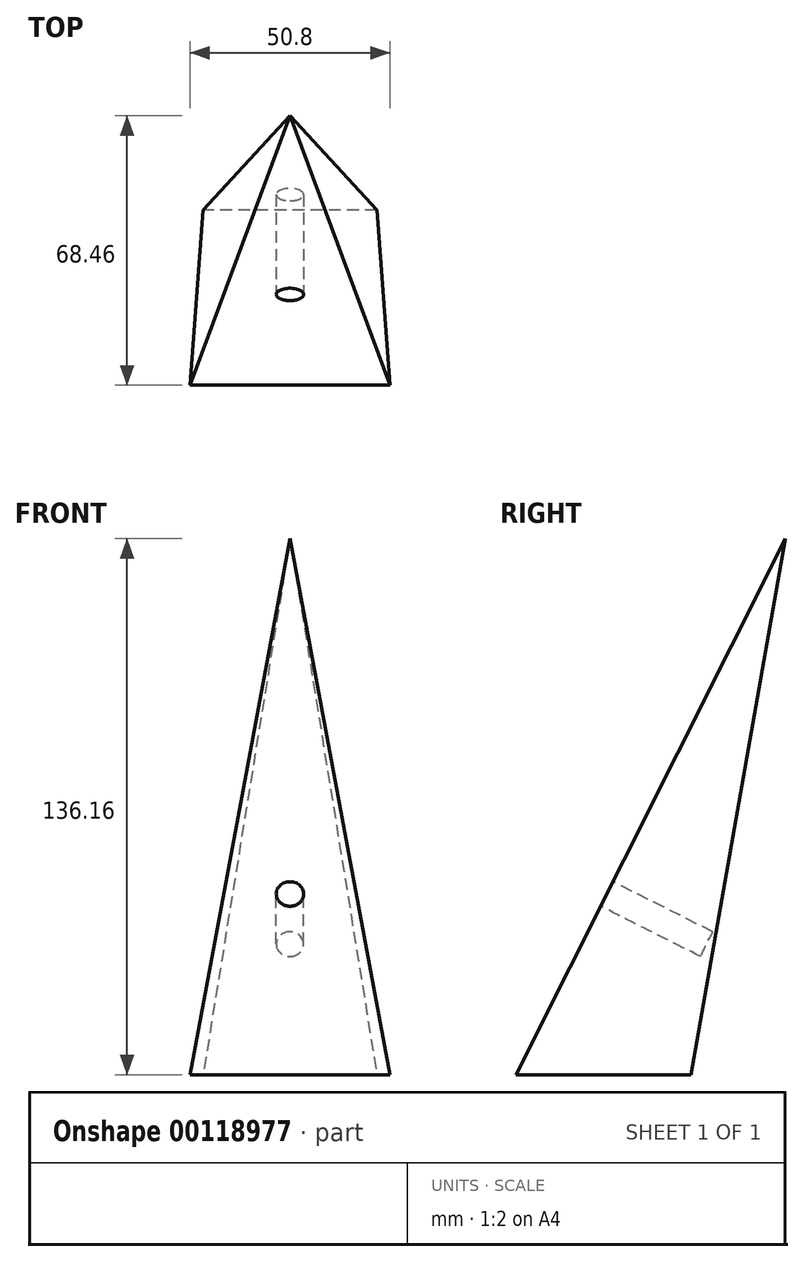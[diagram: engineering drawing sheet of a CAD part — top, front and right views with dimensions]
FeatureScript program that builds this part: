
annotation { "Feature Type Name" : "Feature", "Feature Type Description" : "" }
export const myFeature = defineFeature(function(context is Context, id is Id, definition is map)
    precondition{}
    {
        {
            var Q0;
            Q0=qCreatedBy(makeId("Right.planeOp"),FACE);
            var sketch = newSketch(context, id + "F0", { "sketchPlane" : qUnion([Q0])});
            skLineSegment(sketch, "E0", {"start": v(-22.3, 0) * mm, "end": v(22.16, 0) * mm});
            skLineSegment(sketch, "E1", {"start": v(-22.3, 0) * mm, "end": v(46.17, 136.16) * mm});
            skLineSegment(sketch, "E2", {"start": v(46.17, 136.16) * mm, "end": v(22.16, 0) * mm});
            skSolve(sketch);
        }
        {
            var Q0;
            Q0 = qSketchRegion(id + "F0", true);
            extrude(context, id + "F1", {"entities" : qUnion([Q0]), "depth" : 50.8 * mm});
        }
        {
            var Q0;
            Q0=makeQuery(id+"F1.opExtrude","SWEPT_FACE",FACE,{"disambiguationData":[OSD([sQuery(id+"F0.wireOp",EDGE,"E1")])]});
            var sketch = newSketch(context, id + "F2", { "sketchPlane" : qUnion([Q0])});
            skLineSegment(sketch, "E3", {"start": v(0, -10.01) * mm, "end": v(25.4, 142.39) * mm});
            skLineSegment(sketch, "E4", {"start": v(0, 142.39) * mm, "end": v(0, -10.01) * mm});
            skLineSegment(sketch, "E5", {"start": v(0, 142.39) * mm, "end": v(50.8, 142.39) * mm});
            skLineSegment(sketch, "E6", {"start": v(50.8, 142.39) * mm, "end": v(50.8, -10.01) * mm});
            skLineSegment(sketch, "E7", {"start": v(50.8, -10.01) * mm, "end": v(25.4, 142.39) * mm});
            skSolve(sketch);
        }
        {
            var Q0;
            Q0 = qSketchRegion(id + "F2", true);
            extrude(context, id + "F3", {"entities" : qUnion([Q0]), "operationType" : NewBodyOperationType.REMOVE, "endBound" : BoundingType.THROUGH_ALL, "oppositeDirection" : true, "depth" : 25.4 * mm});
        }
        {
            var Q0;
            Q0=makeQuery(id+"F1.opExtrude","SWEPT_FACE",FACE,{"disambiguationData":[OSD([sQuery(id+"F0.wireOp",EDGE,"E1")])]});
            var sketch = newSketch(context, id + "F4", { "sketchPlane" : qUnion([Q0])});
            skLineSegment(sketch, "E8", {"start": v(25.4, -10.01) * mm, "end": v(25.4, 142.39) * mm, "construction": true});
            skCircle(sketch, "E9", {"center": v(25.4, 41.37) * mm, "radius": 3.5 * mm});
            skSolve(sketch);
        }
        {
            var Q0;
            Q0 = qSketchRegion(id + "F4", true);
            extrude(context, id + "F5", {"entities" : qUnion([Q0]), "operationType" : NewBodyOperationType.REMOVE, "oppositeDirection" : true, "depth" : 28.37 * mm});
        }
    });
